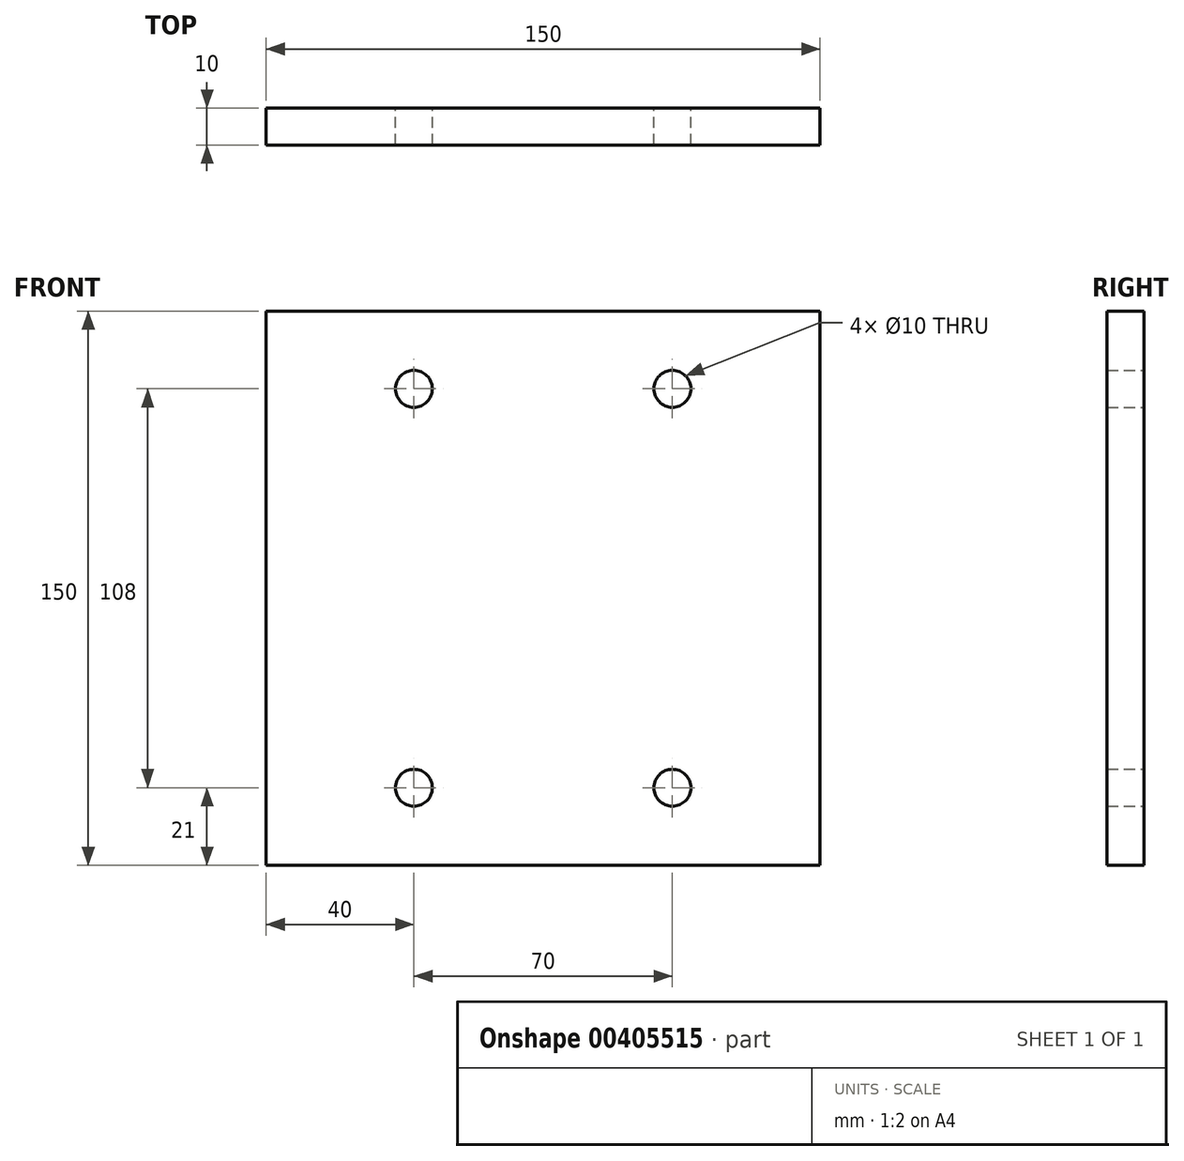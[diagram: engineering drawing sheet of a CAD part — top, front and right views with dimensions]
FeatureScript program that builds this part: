
annotation { "Feature Type Name" : "Feature", "Feature Type Description" : "" }
export const myFeature = defineFeature(function(context is Context, id is Id, definition is map)
    precondition{}
    {
        {
            var Q0;
            Q0=qCreatedBy(makeId("Front.planeOp"),FACE);
            var sketch = newSketch(context, id + "F0", { "sketchPlane" : qUnion([Q0])});
            skLineSegment(sketch, "E0.bottom", {"start": v(75, 75) * mm, "end": v(-75, 75) * mm});
            skLineSegment(sketch, "E0.top", {"start": v(75, -75) * mm, "end": v(-75, -75) * mm});
            skLineSegment(sketch, "E0.left", {"start": v(75, 75) * mm, "end": v(75, -75) * mm});
            skLineSegment(sketch, "E0.right", {"start": v(-75, 75) * mm, "end": v(-75, -75) * mm});
            skPoint(sketch, "E0.middle", {"position": v(0, 0) * mm});
            skCircle(sketch, "E1", {"center": v(-35, 54) * mm, "radius": 5 * mm});
            skCircle(sketch, "E2.0.1.0", {"center": v(-35, -54) * mm, "radius": 5 * mm});
            skCircle(sketch, "E2.1.0.0", {"center": v(35, 54) * mm, "radius": 5 * mm});
            skCircle(sketch, "E2.1.1.0", {"center": v(35, -54) * mm, "radius": 5 * mm});
            skLineSegment(sketch, "E2.direction1", {"start": v(-35, 54) * mm, "end": v(35, 54) * mm, "construction": true});
            skLineSegment(sketch, "E2.direction2", {"start": v(-35, 54) * mm, "end": v(-35, -54) * mm, "construction": true});
            skSolve(sketch);
        }
        {
            var Q0;
            Q0 = qSketchRegion(id + "F0", true);
            extrude(context, id + "F1", {"entities" : qUnion([Q0]), "depth" : 10 * mm});
        }
    });
